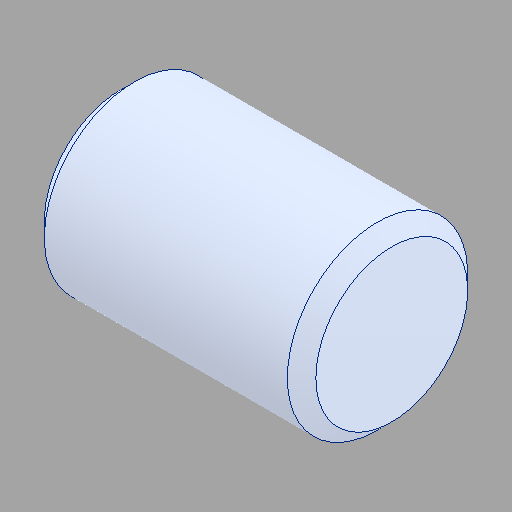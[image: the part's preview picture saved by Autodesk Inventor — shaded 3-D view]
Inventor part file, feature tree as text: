
AUTODESK INVENTOR PART (.ipt)
format: ipt  version: 2024.2 (Build 282272000, 272)  size: 104,960 bytes
history: native  units: in
note: dims shown in document units (in); Inventor stores cm internally (conversion verified against a paired STEP export)
features: chamfer x1
ambient origin geometry x8: Origin, YZ Plane, XZ Plane, XY Plane, X Axis, Y Axis, Z Axis, Center Point
bodies: Solid1 (feature_tree)
feature tree (1):
  chamfer  "Chamfer1"  [1 undecoded]
note: 1 required parameter value undecoded (feature->parameter linkage not recoverable at this tier; creation-order binding heuristic only, values carry confidence <= 0.55)
